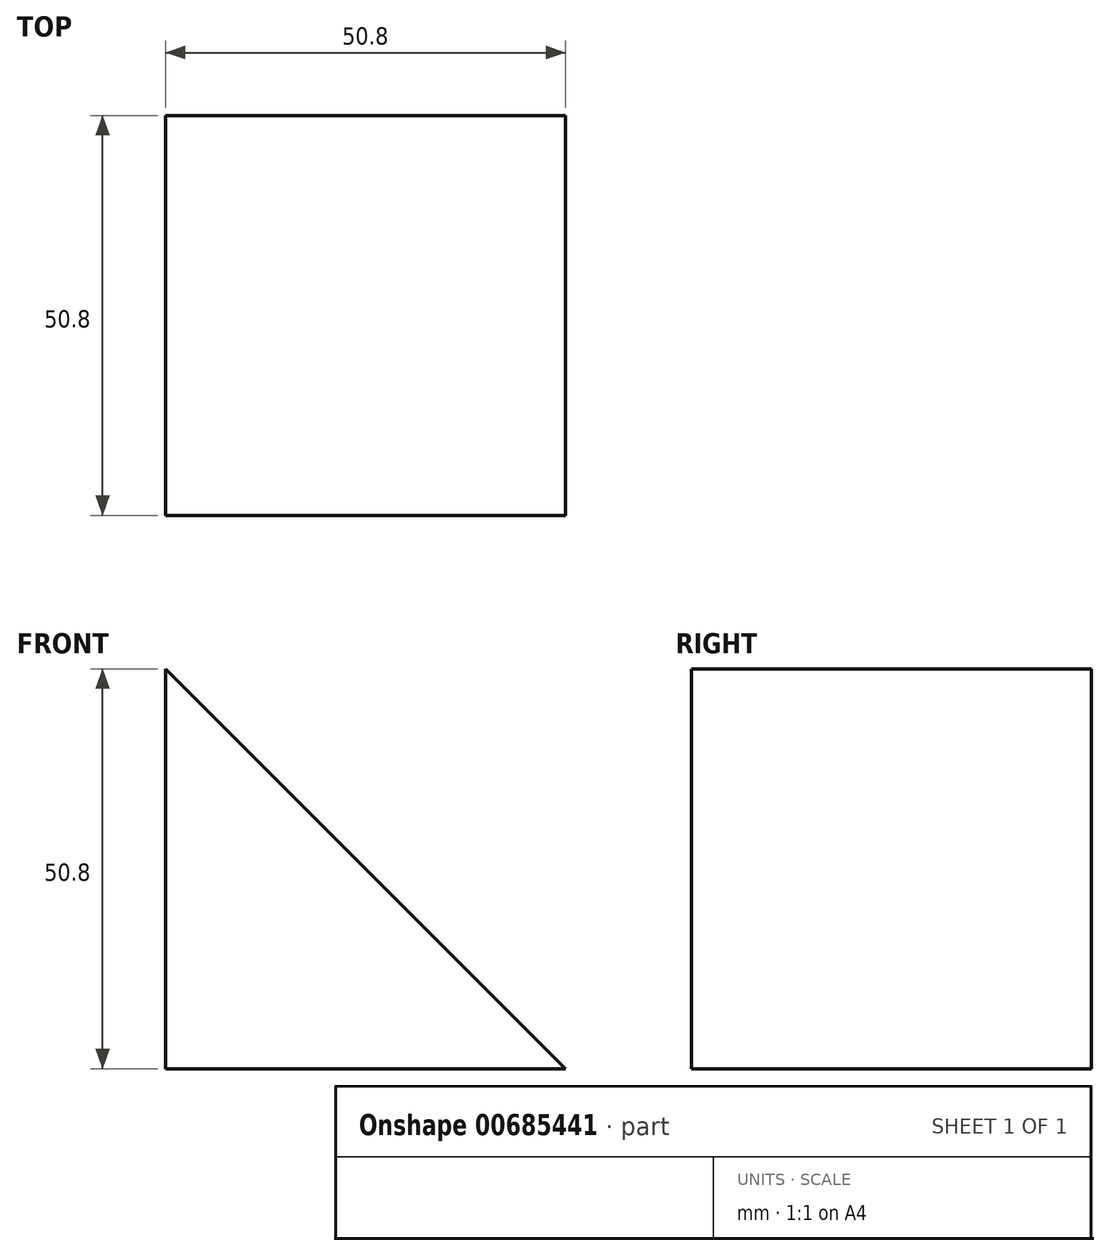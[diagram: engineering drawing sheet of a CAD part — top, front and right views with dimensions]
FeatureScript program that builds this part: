
annotation { "Feature Type Name" : "Feature", "Feature Type Description" : "" }
export const myFeature = defineFeature(function(context is Context, id is Id, definition is map)
    precondition{}
    {
        {
            var Q0;
            Q0=qCreatedBy(makeId("Front.planeOp"),FACE);
            var sketch = newSketch(context, id + "F0", { "sketchPlane" : qUnion([Q0])});
            skLineSegment(sketch, "E0", {"start": v(-54.7, 0) * mm, "end": v(-3.9, 0) * mm});
            skLineSegment(sketch, "E1", {"start": v(-54.7, 0) * mm, "end": v(-54.7, 50.8) * mm});
            skLineSegment(sketch, "E2", {"start": v(-54.7, 50.8) * mm, "end": v(-3.9, 0) * mm});
            skSolve(sketch);
        }
        {
            var Q0;
            Q0 = qSketchRegion(id + "F0", true);
            extrude(context, id + "F1", {"entities" : qUnion([Q0]), "depth" : 50.8 * mm, "offsetDistance" : 25.4 * mm});
        }
    });
